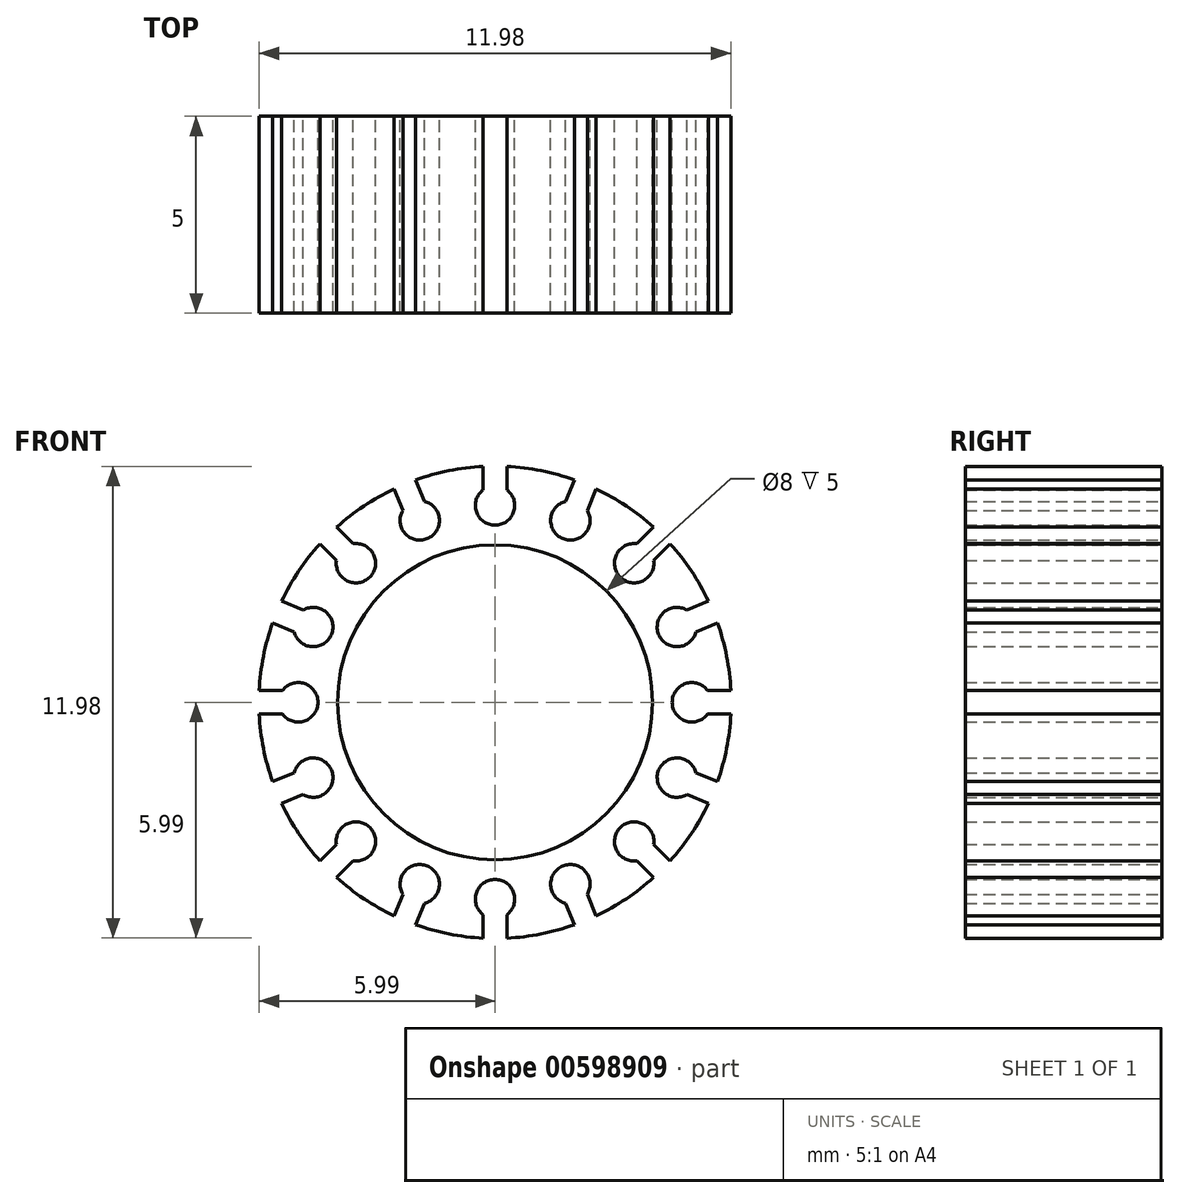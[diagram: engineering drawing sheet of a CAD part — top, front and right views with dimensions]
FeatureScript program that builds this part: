
annotation { "Feature Type Name" : "Feature", "Feature Type Description" : "" }
export const myFeature = defineFeature(function(context is Context, id is Id, definition is map)
    precondition{}
    {
        {
            var Q0;
            Q0=qCreatedBy(makeId("Front.planeOp"),FACE);
            var sketch = newSketch(context, id + "F0", { "sketchPlane" : qUnion([Q0])});
            skCircle(sketch, "E0", {"center": v(0, 0) * mm, "radius": 4 * mm});
            skCircle(sketch, "E1", {"center": v(0, 0) * mm, "radius": 6 * mm});
            skLineSegment(sketch, "E2", {"start": v(0, 0) * mm, "end": v(0, 6) * mm, "construction": true});
            skLineSegment(sketch, "E3.bottom", {"start": v(-0.3, 5) * mm, "end": v(0.3, 5) * mm});
            skLineSegment(sketch, "E3.top", {"start": v(-0.3, 7) * mm, "end": v(0.3, 7) * mm});
            skLineSegment(sketch, "E3.left", {"start": v(-0.3, 5) * mm, "end": v(-0.3, 7) * mm});
            skLineSegment(sketch, "E3.right", {"start": v(0.3, 5) * mm, "end": v(0.3, 7) * mm});
            skPoint(sketch, "E3.middle", {"position": v(0, 6) * mm});
            skLineSegment(sketch, "E4", {"start": v(0, 0) * mm, "end": v(0, 5) * mm, "construction": true});
            skCircle(sketch, "E5", {"center": v(0, 5) * mm, "radius": 0.5 * mm});
            skLineSegment(sketch, "E6.1.0", {"start": v(-2.2, 4.5) * mm, "end": v(-2.96, 6.35) * mm});
            skLineSegment(sketch, "E6.1.1", {"start": v(-1.64, 4.73) * mm, "end": v(-2.4, 6.58) * mm});
            skLineSegment(sketch, "E6.1.2", {"start": v(-2.96, 6.35) * mm, "end": v(-2.4, 6.58) * mm});
            skLineSegment(sketch, "E6.1.3", {"start": v(-2.2, 4.5) * mm, "end": v(-1.64, 4.73) * mm});
            skCircle(sketch, "E6.1.4", {"center": v(-1.91, 4.62) * mm, "radius": 0.5 * mm});
            skLineSegment(sketch, "E6.2.0", {"start": v(-3.75, 3.32) * mm, "end": v(-5.16, 4.74) * mm});
            skLineSegment(sketch, "E6.2.1", {"start": v(-3.32, 3.75) * mm, "end": v(-4.74, 5.16) * mm});
            skLineSegment(sketch, "E6.2.2", {"start": v(-5.16, 4.74) * mm, "end": v(-4.74, 5.16) * mm});
            skLineSegment(sketch, "E6.2.3", {"start": v(-3.75, 3.32) * mm, "end": v(-3.32, 3.75) * mm});
            skCircle(sketch, "E6.2.4", {"center": v(-3.54, 3.54) * mm, "radius": 0.5 * mm});
            skLineSegment(sketch, "E7.1.3.0", {"start": v(-4.73, 1.64) * mm, "end": v(-6.58, 2.4) * mm});
            skLineSegment(sketch, "E7.3.3.0", {"start": v(-4.5, 2.2) * mm, "end": v(-6.35, 2.96) * mm});
            skLineSegment(sketch, "E7.6.3.0", {"start": v(-6.58, 2.4) * mm, "end": v(-6.35, 2.96) * mm});
            skLineSegment(sketch, "E7.9.3.0", {"start": v(-4.73, 1.64) * mm, "end": v(-4.5, 2.2) * mm});
            skCircle(sketch, "E7.12.3.0", {"center": v(-4.62, 1.91) * mm, "radius": 0.5 * mm});
            skLineSegment(sketch, "E7.1.4.0", {"start": v(-5, -0.3) * mm, "end": v(-7, -0.3) * mm});
            skLineSegment(sketch, "E7.3.4.0", {"start": v(-5, 0.3) * mm, "end": v(-7, 0.3) * mm});
            skLineSegment(sketch, "E7.6.4.0", {"start": v(-7, -0.3) * mm, "end": v(-7, 0.3) * mm});
            skLineSegment(sketch, "E7.9.4.0", {"start": v(-5, -0.3) * mm, "end": v(-5, 0.3) * mm});
            skCircle(sketch, "E7.12.4.0", {"center": v(-5, 0) * mm, "radius": 0.5 * mm});
            skLineSegment(sketch, "E7.1.5.0", {"start": v(-4.5, -2.2) * mm, "end": v(-6.35, -2.96) * mm});
            skLineSegment(sketch, "E7.3.5.0", {"start": v(-4.73, -1.64) * mm, "end": v(-6.58, -2.4) * mm});
            skLineSegment(sketch, "E7.6.5.0", {"start": v(-6.35, -2.96) * mm, "end": v(-6.58, -2.4) * mm});
            skLineSegment(sketch, "E7.9.5.0", {"start": v(-4.5, -2.2) * mm, "end": v(-4.73, -1.64) * mm});
            skCircle(sketch, "E7.12.5.0", {"center": v(-4.62, -1.91) * mm, "radius": 0.5 * mm});
            skLineSegment(sketch, "E7.1.6.0", {"start": v(-3.32, -3.75) * mm, "end": v(-4.74, -5.16) * mm});
            skLineSegment(sketch, "E7.3.6.0", {"start": v(-3.75, -3.32) * mm, "end": v(-5.16, -4.74) * mm});
            skLineSegment(sketch, "E7.6.6.0", {"start": v(-4.74, -5.16) * mm, "end": v(-5.16, -4.74) * mm});
            skLineSegment(sketch, "E7.9.6.0", {"start": v(-3.32, -3.75) * mm, "end": v(-3.75, -3.32) * mm});
            skCircle(sketch, "E7.12.6.0", {"center": v(-3.54, -3.54) * mm, "radius": 0.5 * mm});
            skLineSegment(sketch, "E7.1.7.0", {"start": v(-1.64, -4.73) * mm, "end": v(-2.4, -6.58) * mm});
            skLineSegment(sketch, "E7.3.7.0", {"start": v(-2.2, -4.5) * mm, "end": v(-2.96, -6.35) * mm});
            skLineSegment(sketch, "E7.6.7.0", {"start": v(-2.4, -6.58) * mm, "end": v(-2.96, -6.35) * mm});
            skLineSegment(sketch, "E7.9.7.0", {"start": v(-1.64, -4.73) * mm, "end": v(-2.2, -4.5) * mm});
            skCircle(sketch, "E7.12.7.0", {"center": v(-1.91, -4.62) * mm, "radius": 0.5 * mm});
            skLineSegment(sketch, "E7.1.8.0", {"start": v(0.3, -5) * mm, "end": v(0.3, -7) * mm});
            skLineSegment(sketch, "E7.3.8.0", {"start": v(-0.3, -5) * mm, "end": v(-0.3, -7) * mm});
            skLineSegment(sketch, "E7.6.8.0", {"start": v(0.3, -7) * mm, "end": v(-0.3, -7) * mm});
            skLineSegment(sketch, "E7.9.8.0", {"start": v(0.3, -5) * mm, "end": v(-0.3, -5) * mm});
            skCircle(sketch, "E7.12.8.0", {"center": v(0, -5) * mm, "radius": 0.5 * mm});
            skLineSegment(sketch, "E7.1.9.0", {"start": v(2.2, -4.5) * mm, "end": v(2.96, -6.35) * mm});
            skLineSegment(sketch, "E7.3.9.0", {"start": v(1.64, -4.73) * mm, "end": v(2.4, -6.58) * mm});
            skLineSegment(sketch, "E7.6.9.0", {"start": v(2.96, -6.35) * mm, "end": v(2.4, -6.58) * mm});
            skLineSegment(sketch, "E7.9.9.0", {"start": v(2.2, -4.5) * mm, "end": v(1.64, -4.73) * mm});
            skCircle(sketch, "E7.12.9.0", {"center": v(1.91, -4.62) * mm, "radius": 0.5 * mm});
            skLineSegment(sketch, "E7.1.10.0", {"start": v(3.75, -3.32) * mm, "end": v(5.16, -4.74) * mm});
            skLineSegment(sketch, "E7.3.10.0", {"start": v(3.32, -3.75) * mm, "end": v(4.74, -5.16) * mm});
            skLineSegment(sketch, "E7.6.10.0", {"start": v(5.16, -4.74) * mm, "end": v(4.74, -5.16) * mm});
            skLineSegment(sketch, "E7.9.10.0", {"start": v(3.75, -3.32) * mm, "end": v(3.32, -3.75) * mm});
            skCircle(sketch, "E7.12.10.0", {"center": v(3.54, -3.54) * mm, "radius": 0.5 * mm});
            skLineSegment(sketch, "E7.1.11.0", {"start": v(4.73, -1.64) * mm, "end": v(6.58, -2.4) * mm});
            skLineSegment(sketch, "E7.3.11.0", {"start": v(4.5, -2.2) * mm, "end": v(6.35, -2.96) * mm});
            skLineSegment(sketch, "E7.6.11.0", {"start": v(6.58, -2.4) * mm, "end": v(6.35, -2.96) * mm});
            skLineSegment(sketch, "E7.9.11.0", {"start": v(4.73, -1.64) * mm, "end": v(4.5, -2.2) * mm});
            skCircle(sketch, "E7.12.11.0", {"center": v(4.62, -1.91) * mm, "radius": 0.5 * mm});
            skLineSegment(sketch, "E7.1.12.0", {"start": v(5, 0.3) * mm, "end": v(7, 0.3) * mm});
            skLineSegment(sketch, "E7.3.12.0", {"start": v(5, -0.3) * mm, "end": v(7, -0.3) * mm});
            skLineSegment(sketch, "E7.6.12.0", {"start": v(7, 0.3) * mm, "end": v(7, -0.3) * mm});
            skLineSegment(sketch, "E7.9.12.0", {"start": v(5, 0.3) * mm, "end": v(5, -0.3) * mm});
            skCircle(sketch, "E7.12.12.0", {"center": v(5, 0) * mm, "radius": 0.5 * mm});
            skLineSegment(sketch, "E7.1.13.0", {"start": v(4.5, 2.2) * mm, "end": v(6.35, 2.96) * mm});
            skLineSegment(sketch, "E7.3.13.0", {"start": v(4.73, 1.64) * mm, "end": v(6.58, 2.4) * mm});
            skLineSegment(sketch, "E7.6.13.0", {"start": v(6.35, 2.96) * mm, "end": v(6.58, 2.4) * mm});
            skLineSegment(sketch, "E7.9.13.0", {"start": v(4.5, 2.2) * mm, "end": v(4.73, 1.64) * mm});
            skCircle(sketch, "E7.12.13.0", {"center": v(4.62, 1.91) * mm, "radius": 0.5 * mm});
            skLineSegment(sketch, "E7.1.14.0", {"start": v(3.32, 3.75) * mm, "end": v(4.74, 5.16) * mm});
            skLineSegment(sketch, "E7.3.14.0", {"start": v(3.75, 3.32) * mm, "end": v(5.16, 4.74) * mm});
            skLineSegment(sketch, "E7.6.14.0", {"start": v(4.74, 5.16) * mm, "end": v(5.16, 4.74) * mm});
            skLineSegment(sketch, "E7.9.14.0", {"start": v(3.32, 3.75) * mm, "end": v(3.75, 3.32) * mm});
            skCircle(sketch, "E7.12.14.0", {"center": v(3.54, 3.54) * mm, "radius": 0.5 * mm});
            skLineSegment(sketch, "E7.1.15.0", {"start": v(1.64, 4.73) * mm, "end": v(2.4, 6.58) * mm});
            skLineSegment(sketch, "E7.3.15.0", {"start": v(2.2, 4.5) * mm, "end": v(2.96, 6.35) * mm});
            skLineSegment(sketch, "E7.6.15.0", {"start": v(2.4, 6.58) * mm, "end": v(2.96, 6.35) * mm});
            skLineSegment(sketch, "E7.9.15.0", {"start": v(1.64, 4.73) * mm, "end": v(2.2, 4.5) * mm});
            skCircle(sketch, "E7.12.15.0", {"center": v(1.91, 4.62) * mm, "radius": 0.5 * mm});
            skSolve(sketch);
        }
        {
            var Q0;
            Q0=makeQuery(id+"F0.imprint","IMPRINT",FACE,{"disambiguationData":[TD([[makeQuery(id+"F0.imprint","IMPRINT",EDGE,{"derivedFrom":sQuery(id+"F0.wireOp",EDGE,"E0")}),-1.0]])]});
            extrude(context, id + "F1", {"entities" : qUnion([Q0]), "depth" : 5 * mm, "offsetDistance" : 25 * mm});
        }
    });
